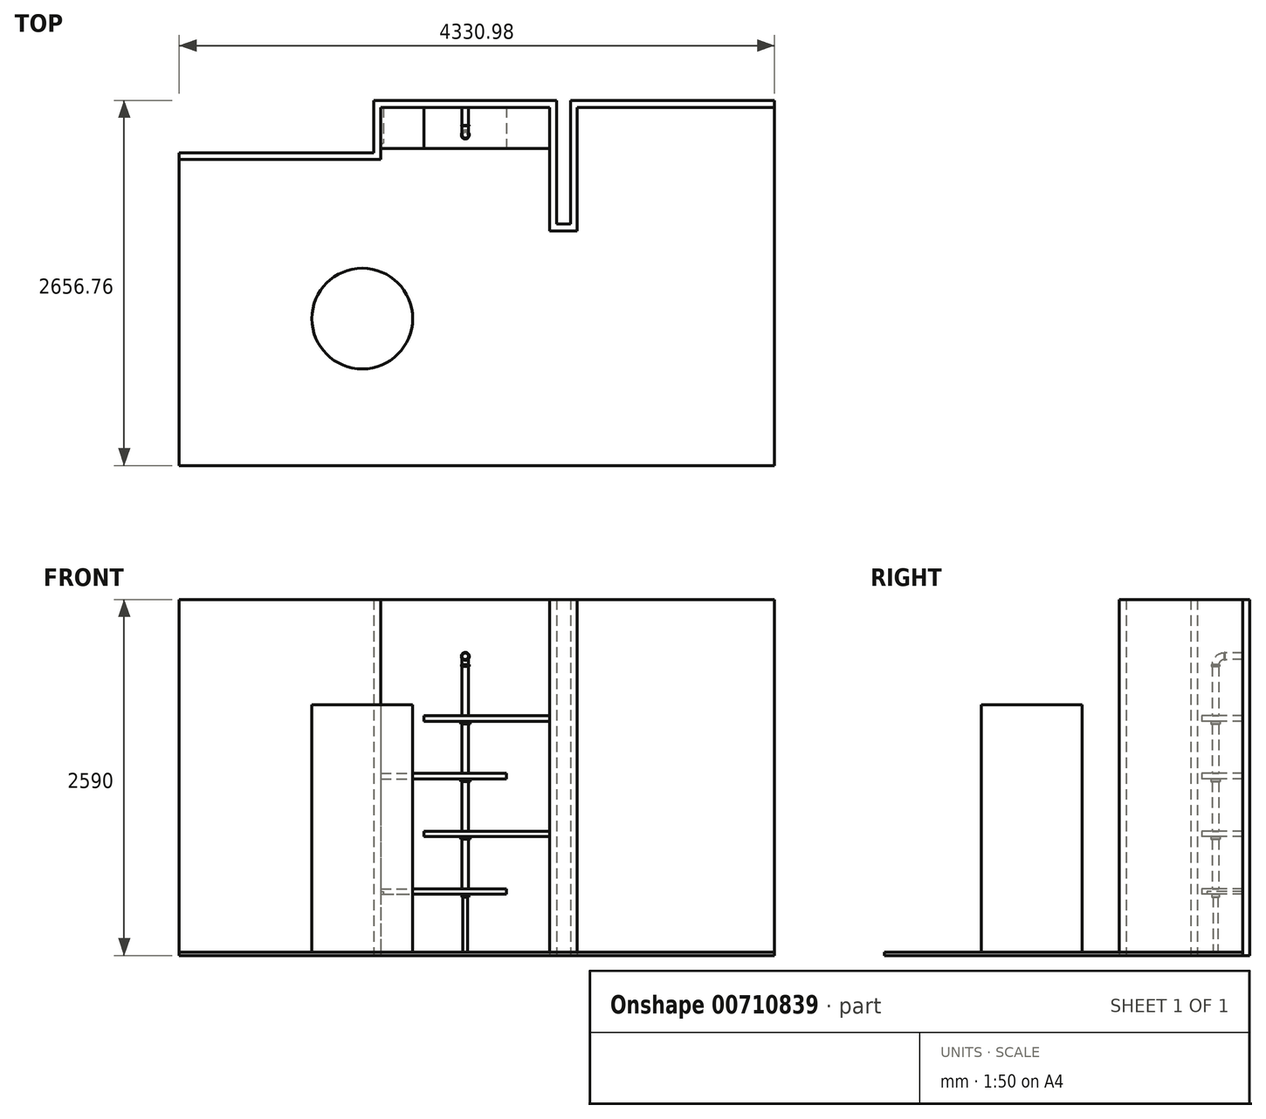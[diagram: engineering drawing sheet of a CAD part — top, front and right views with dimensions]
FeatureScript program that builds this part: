
annotation { "Feature Type Name" : "Feature", "Feature Type Description" : "" }
export const myFeature = defineFeature(function(context is Context, id is Id, definition is map)
    precondition{}
    {
        {
            var Q0;
            Q0=qCreatedBy(makeId("Top.planeOp"),FACE);
            var sketch = newSketch(context, id + "F0", { "sketchPlane" : qUnion([Q0])});
            skLineSegment(sketch, "E0", {"start": v(-2171.4, 181.95) * mm, "end": v(-705.2, 181.95) * mm});
            skLineSegment(sketch, "E1", {"start": v(-705.2, 181.95) * mm, "end": v(-705.2, 561.95) * mm});
            skLineSegment(sketch, "E2", {"start": v(-705.2, 561.95) * mm, "end": v(524.8, 561.95) * mm});
            skLineSegment(sketch, "E3", {"start": v(524.8, 561.95) * mm, "end": v(524.8, -338.05) * mm});
            skLineSegment(sketch, "E4", {"start": v(524.8, -338.05) * mm, "end": v(724.8, -338.05) * mm});
            skLineSegment(sketch, "E5", {"start": v(724.8, -338.05) * mm, "end": v(724.8, 561.95) * mm});
            skLineSegment(sketch, "E6", {"start": v(724.8, 561.95) * mm, "end": v(2159.6, 561.95) * mm});
            skLineSegment(sketch, "E7", {"start": v(2159.6, 561.95) * mm, "end": v(2159.6, -2044.81) * mm});
            skLineSegment(sketch, "E8", {"start": v(2159.6, -2044.81) * mm, "end": v(-2171.4, -2044.81) * mm});
            skLineSegment(sketch, "E9", {"start": v(-2171.4, -2044.81) * mm, "end": v(-2171.4, 181.95) * mm});
            skSolve(sketch);
        }
        {
            var Q0;
            Q0=makeQuery(id+"F0.imprint","IMPRINT",FACE,{"disambiguationData":[TD([[makeQuery(id+"F0.imprint","IMPRINT",EDGE,{"derivedFrom":sQuery(id+"F0.wireOp",EDGE,"E0")}),-1.0]])]});
            extrude(context, id + "F1", {"entities" : qUnion([Q0]), "depth" : 25 * mm, "offsetDistance" : 25 * mm});
        }
        {
            var Q0;
            Q0=makeQuery(id+"F1.opExtrude","CAP_FACE",FACE,{"disambiguationData":[OSD([sQuery(id+"F0.wireOp",EDGE,"E0"),sQuery(id+"F0.wireOp",EDGE,"E1"),sQuery(id+"F0.wireOp",EDGE,"E2"),sQuery(id+"F0.wireOp",EDGE,"E3"),sQuery(id+"F0.wireOp",EDGE,"E4"),sQuery(id+"F0.wireOp",EDGE,"E5"),sQuery(id+"F0.wireOp",EDGE,"E6"),sQuery(id+"F0.wireOp",EDGE,"E7"),sQuery(id+"F0.wireOp",EDGE,"E8"),sQuery(id+"F0.wireOp",EDGE,"E9")])],"isStart":true});
            var sketch = newSketch(context, id + "F2", { "sketchPlane" : qUnion([Q0])});
            skLineSegment(sketch, "E10", {"start": v(-2171.4, -181.95) * mm, "end": v(-705.2, -181.95) * mm});
            skLineSegment(sketch, "E11", {"start": v(-705.2, -181.95) * mm, "end": v(-705.2, -561.95) * mm});
            skLineSegment(sketch, "E12", {"start": v(-705.2, -561.95) * mm, "end": v(524.8, -561.95) * mm});
            skLineSegment(sketch, "E13", {"start": v(524.8, -561.95) * mm, "end": v(524.8, 338.05) * mm});
            skLineSegment(sketch, "E14", {"start": v(524.8, 338.05) * mm, "end": v(724.8, 338.05) * mm});
            skLineSegment(sketch, "E15", {"start": v(724.8, 338.05) * mm, "end": v(724.8, -561.95) * mm});
            skLineSegment(sketch, "E16", {"start": v(724.8, -561.95) * mm, "end": v(2159.6, -561.95) * mm});
            skLineSegment(sketch, "E17", {"start": v(2159.6, -561.95) * mm, "end": v(2159.6, -611.95) * mm});
            skLineSegment(sketch, "E18", {"start": v(2159.6, -611.95) * mm, "end": v(674.8, -611.95) * mm});
            skLineSegment(sketch, "E19", {"start": v(674.8, -611.95) * mm, "end": v(674.8, 288.05) * mm});
            skLineSegment(sketch, "E20", {"start": v(674.8, 288.05) * mm, "end": v(574.8, 288.05) * mm});
            skLineSegment(sketch, "E21", {"start": v(574.8, 288.05) * mm, "end": v(574.8, -611.95) * mm});
            skLineSegment(sketch, "E22", {"start": v(574.8, -611.95) * mm, "end": v(-755.2, -611.95) * mm});
            skLineSegment(sketch, "E23", {"start": v(-755.2, -611.95) * mm, "end": v(-755.2, -231.95) * mm});
            skLineSegment(sketch, "E24", {"start": v(-755.2, -231.95) * mm, "end": v(-2171.4, -231.95) * mm});
            skLineSegment(sketch, "E25", {"start": v(-2171.4, -231.95) * mm, "end": v(-2171.4, -181.95) * mm});
            skSolve(sketch);
        }
        {
            var Q0;
            Q0=makeQuery(id+"F2.imprint","IMPRINT",FACE,{"disambiguationData":[TD([[makeQuery(id+"F2.imprint","IMPRINT",EDGE,{"derivedFrom":sQuery(id+"F2.wireOp",EDGE,"E10")}),-1.0]])]});
            extrude(context, id + "F3", {"entities" : qUnion([Q0]), "oppositeDirection" : true, "depth" : 2590 * mm, "offsetDistance" : 25 * mm});
        }
        {
            var Q0;
            Q0=makeQuery(id+"F1.opExtrude","CAP_FACE",FACE,{"disambiguationData":[OSD([sQuery(id+"F0.wireOp",EDGE,"E0"),sQuery(id+"F0.wireOp",EDGE,"E1"),sQuery(id+"F0.wireOp",EDGE,"E2"),sQuery(id+"F0.wireOp",EDGE,"E3"),sQuery(id+"F0.wireOp",EDGE,"E4"),sQuery(id+"F0.wireOp",EDGE,"E5"),sQuery(id+"F0.wireOp",EDGE,"E6"),sQuery(id+"F0.wireOp",EDGE,"E7"),sQuery(id+"F0.wireOp",EDGE,"E8"),sQuery(id+"F0.wireOp",EDGE,"E9")])],"isStart":false});
            var sketch = newSketch(context, id + "F4", { "sketchPlane" : qUnion([Q0])});
            skLineSegment(sketch, "E26.bottom", {"start": v(-705.2, 561.95) * mm, "end": v(349.8, 561.95) * mm});
            skLineSegment(sketch, "E26.top", {"start": v(-705.2, 215.3) * mm, "end": v(349.8, 215.3) * mm});
            skLineSegment(sketch, "E26.left", {"start": v(-705.2, 561.95) * mm, "end": v(-705.2, 215.3) * mm});
            skLineSegment(sketch, "E26.right", {"start": v(349.8, 561.95) * mm, "end": v(349.8, 215.3) * mm});
            skCircle(sketch, "E27", {"center": v(-90.2, 361.95) * mm, "radius": 27 * mm});
            skPoint(sketch, "E27.centerSnap0", {"position": v(-90.2, 561.95) * mm});
            skSolve(sketch);
        }
        {
            var Q0;
            {var subQ3=sQuery(id+"F4.wireOp",EDGE,"E26.top");Q0=makeQuery(id+"F4.imprint","IMPRINT",FACE,{"disambiguationData":[TD([[makeQuery(id+"F4.imprint","IMPRINT",EDGE,{"derivedFrom":subQ3}),-1.0]])]});}
            cPlane(context, id + "F5", {"entities" : qUnion([Q0]), "cplaneType" : CPlaneType.OFFSET, "offset" : 420 * mm, "width" : 150 * mm, "height" : 150 * mm});
        }
        {
            var Q0;
            Q0=qCreatedBy(id+"F5.planeOp",FACE);
            cPlane(context, id + "F6", {"entities" : qUnion([Q0]), "cplaneType" : CPlaneType.OFFSET, "offset" : 420 * mm, "width" : 150 * mm, "height" : 150 * mm});
        }
        {
            var Q0;
            Q0=qCreatedBy(id+"F6.planeOp",FACE);
            cPlane(context, id + "F7", {"entities" : qUnion([Q0]), "cplaneType" : CPlaneType.OFFSET, "offset" : 420 * mm, "width" : 150 * mm, "height" : 150 * mm});
        }
        {
            var Q0;
            Q0=qCreatedBy(id+"F7.planeOp",FACE);
            cPlane(context, id + "F8", {"entities" : qUnion([Q0]), "cplaneType" : CPlaneType.OFFSET, "offset" : 420 * mm, "width" : 150 * mm, "height" : 150 * mm});
        }
        {
            var Q0;
            Q0=qCreatedBy(id+"F5.planeOp",FACE);
            var sketch = newSketch(context, id + "F9", { "sketchPlane" : qUnion([Q0])});
            skLineSegment(sketch, "E28.bottom", {"start": v(-705.2, 561.95) * mm, "end": v(209.8, 561.95) * mm});
            skLineSegment(sketch, "E28.top", {"start": v(-705.2, 261.95) * mm, "end": v(209.8, 261.95) * mm});
            skLineSegment(sketch, "E28.left", {"start": v(-705.2, 561.95) * mm, "end": v(-705.2, 261.95) * mm});
            skLineSegment(sketch, "E28.right", {"start": v(209.8, 561.95) * mm, "end": v(209.8, 261.95) * mm});
            skSolve(sketch);
        }
        {
            var Q0;
            Q0 = qSketchRegion(id + "F9", true);
            extrude(context, id + "F10", {"entities" : qUnion([Q0]), "depth" : 40 * mm, "offsetDistance" : 25 * mm});
        }
        {
            var Q0;
            Q0=qCreatedBy(id+"F6.planeOp",FACE);
            var sketch = newSketch(context, id + "F11", { "sketchPlane" : qUnion([Q0])});
            skLineSegment(sketch, "E29.bottom", {"start": v(524.8, 561.95) * mm, "end": v(-390.2, 561.95) * mm});
            skLineSegment(sketch, "E29.top", {"start": v(524.8, 261.95) * mm, "end": v(-390.2, 261.95) * mm});
            skLineSegment(sketch, "E29.left", {"start": v(524.8, 561.95) * mm, "end": v(524.8, 261.95) * mm});
            skLineSegment(sketch, "E29.right", {"start": v(-390.2, 561.95) * mm, "end": v(-390.2, 261.95) * mm});
            skSolve(sketch);
        }
        {
            var Q0;
            Q0 = qSketchRegion(id + "F11", true);
            extrude(context, id + "F12", {"entities" : qUnion([Q0]), "depth" : 40 * mm, "offsetDistance" : 25 * mm});
        }
        {
            var Q0;
            Q0=qCreatedBy(id+"F7.planeOp",FACE);
            var sketch = newSketch(context, id + "F13", { "sketchPlane" : qUnion([Q0])});
            skLineSegment(sketch, "E30.bottom", {"start": v(-705.2, 561.95) * mm, "end": v(209.8, 561.95) * mm});
            skLineSegment(sketch, "E30.top", {"start": v(-705.2, 261.95) * mm, "end": v(209.8, 261.95) * mm});
            skLineSegment(sketch, "E30.left", {"start": v(-705.2, 561.95) * mm, "end": v(-705.2, 261.95) * mm});
            skLineSegment(sketch, "E30.right", {"start": v(209.8, 561.95) * mm, "end": v(209.8, 261.95) * mm});
            skSolve(sketch);
        }
        {
            var Q0;
            Q0 = qSketchRegion(id + "F13", true);
            extrude(context, id + "F14", {"entities" : qUnion([Q0]), "depth" : 40 * mm, "offsetDistance" : 25 * mm});
        }
        {
            var Q0;
            Q0=qCreatedBy(id+"F8.planeOp",FACE);
            var sketch = newSketch(context, id + "F15", { "sketchPlane" : qUnion([Q0])});
            skLineSegment(sketch, "E31.bottom", {"start": v(524.8, 561.95) * mm, "end": v(-390.2, 561.95) * mm});
            skLineSegment(sketch, "E31.top", {"start": v(524.8, 261.95) * mm, "end": v(-390.2, 261.95) * mm});
            skLineSegment(sketch, "E31.left", {"start": v(524.8, 561.95) * mm, "end": v(524.8, 261.95) * mm});
            skLineSegment(sketch, "E31.right", {"start": v(-390.2, 561.95) * mm, "end": v(-390.2, 261.95) * mm});
            skSolve(sketch);
        }
        {
            var Q0;
            Q0 = qSketchRegion(id + "F15", true);
            extrude(context, id + "F16", {"entities" : qUnion([Q0]), "depth" : 40 * mm, "offsetDistance" : 25 * mm});
        }
        {
            var Q0;
            {var subQ3=sQuery(id+"F4.wireOp",EDGE,"E26.top");Q0=makeQuery(id+"F4.imprint","IMPRINT",FACE,{"disambiguationData":[TD([[makeQuery(id+"F4.imprint","IMPRINT",EDGE,{"derivedFrom":subQ3}),-1.0]])]});}
            var sketch = newSketch(context, id + "F17", { "sketchPlane" : qUnion([Q0])});
            skCircle(sketch, "E32", {"center": v(-90.2, 361.95) * mm, "radius": 18.15 * mm});
            skSolve(sketch);
        }
        {
            var Q0;
            Q0 = qSketchRegion(id + "F17", true);
            extrude(context, id + "F18", {"entities" : qUnion([Q0]), "depth" : 400 * mm, "offsetDistance" : 25 * mm});
        }
        {
            var Q0;
            Q0=makeQuery(id+"F16.opExtrude","CAP_FACE",FACE,{"disambiguationData":[OSD([sQuery(id+"F15.wireOp",EDGE,"E31.bottom"),sQuery(id+"F15.wireOp",EDGE,"E31.top"),sQuery(id+"F15.wireOp",EDGE,"E31.left"),sQuery(id+"F15.wireOp",EDGE,"E31.right")])],"isStart":false});
            var sketch = newSketch(context, id + "F19", { "sketchPlane" : qUnion([Q0])});
            skCircle(sketch, "E33", {"center": v(-90.2, 361.95) * mm, "radius": 24.15 * mm});
            skSolve(sketch);
        }
        {
            var Q0;
            Q0 = qSketchRegion(id + "F19", true);
            extrude(context, id + "F20", {"entities" : qUnion([Q0]), "operationType" : NewBodyOperationType.REMOVE, "oppositeDirection" : true, "depth" : 1320 * mm, "offsetDistance" : 25 * mm});
        }
        {
            var Q0;
            Q0=makeQuery(id+"F18.opExtrude","CAP_FACE",FACE,{"disambiguationData":[OSD([sQuery(id+"F17.wireOp",EDGE,"E32")])],"isStart":false});
            var sketch = newSketch(context, id + "F21", { "sketchPlane" : qUnion([Q0])});
            skCircle(sketch, "E34", {"center": v(-90.2, 361.95) * mm, "radius": 26 * mm});
            skSolve(sketch);
        }
        {
            var Q0;
            Q0 = qSketchRegion(id + "F21", true);
            extrude(context, id + "F22", {"entities" : qUnion([Q0]), "operationType" : NewBodyOperationType.ADD, "depth" : 20 * mm, "offsetDistance" : 25 * mm});
        }
        {
            var Q0;
            Q0=makeQuery(id+"F22.opExtrude","CAP_FACE",FACE,{"disambiguationData":[OSD([sQuery(id+"F21.wireOp",EDGE,"E34")])],"isStart":false});
            var sketch = newSketch(context, id + "F23", { "sketchPlane" : qUnion([Q0])});
            skCircle(sketch, "E35", {"center": v(-90.2, 361.95) * mm, "radius": 24.15 * mm});
            skSolve(sketch);
        }
        {
            var Q0;
            Q0 = qSketchRegion(id + "F23", true);
            extrude(context, id + "F24", {"entities" : qUnion([Q0]), "operationType" : NewBodyOperationType.ADD, "depth" : 400 * mm, "offsetDistance" : 25 * mm});
        }
        {
            var Q0;
            Q0=makeQuery(id+"F24.opExtrude","CAP_FACE",FACE,{"disambiguationData":[OSD([sQuery(id+"F23.wireOp",EDGE,"E35")])],"isStart":false});
            var sketch = newSketch(context, id + "F25", { "sketchPlane" : qUnion([Q0])});
            skCircle(sketch, "E36", {"center": v(-90.2, 361.95) * mm, "radius": 34.15 * mm});
            skSolve(sketch);
        }
        {
            var Q0;
            Q0 = qSketchRegion(id + "F25", true);
            extrude(context, id + "F26", {"entities" : qUnion([Q0]), "operationType" : NewBodyOperationType.ADD, "depth" : 20 * mm, "offsetDistance" : 25 * mm});
        }
        {
            var Q0;
            Q0=makeQuery(id+"F26.opExtrude","CAP_FACE",FACE,{"disambiguationData":[OSD([sQuery(id+"F25.wireOp",EDGE,"E36")])],"isStart":false});
            var sketch = newSketch(context, id + "F27", { "sketchPlane" : qUnion([Q0])});
            skCircle(sketch, "E37", {"center": v(-90.2, 361.95) * mm, "radius": 24.15 * mm});
            skSolve(sketch);
        }
        {
            var Q0;
            Q0 = qSketchRegion(id + "F27", true);
            extrude(context, id + "F28", {"entities" : qUnion([Q0]), "operationType" : NewBodyOperationType.ADD, "depth" : 400 * mm, "offsetDistance" : 25 * mm});
        }
        {
            var Q0;
            Q0=makeQuery(id+"F28.opExtrude","CAP_FACE",FACE,{"disambiguationData":[OSD([sQuery(id+"F27.wireOp",EDGE,"E37")])],"isStart":false});
            var sketch = newSketch(context, id + "F29", { "sketchPlane" : qUnion([Q0])});
            skCircle(sketch, "E38", {"center": v(-90.2, 361.95) * mm, "radius": 34.15 * mm});
            skSolve(sketch);
        }
        {
            var Q0;
            Q0 = qSketchRegion(id + "F29", true);
            extrude(context, id + "F30", {"entities" : qUnion([Q0]), "operationType" : NewBodyOperationType.ADD, "depth" : 20 * mm, "offsetDistance" : 25 * mm});
        }
        {
            var Q0;
            Q0=makeQuery(id+"F30.opExtrude","CAP_FACE",FACE,{"disambiguationData":[OSD([sQuery(id+"F29.wireOp",EDGE,"E38")])],"isStart":false});
            var sketch = newSketch(context, id + "F31", { "sketchPlane" : qUnion([Q0])});
            skCircle(sketch, "E39", {"center": v(-90.2, 361.95) * mm, "radius": 24.15 * mm});
            skSolve(sketch);
        }
        {
            var Q0;
            Q0 = qSketchRegion(id + "F31", true);
            extrude(context, id + "F32", {"entities" : qUnion([Q0]), "operationType" : NewBodyOperationType.ADD, "depth" : 400 * mm, "offsetDistance" : 25 * mm});
        }
        {
            var Q0;
            Q0=makeQuery(id+"F32.opExtrude","CAP_FACE",FACE,{"disambiguationData":[OSD([sQuery(id+"F31.wireOp",EDGE,"E39")])],"isStart":false});
            var sketch = newSketch(context, id + "F33", { "sketchPlane" : qUnion([Q0])});
            skCircle(sketch, "E40", {"center": v(-90.2, 361.95) * mm, "radius": 34.15 * mm});
            skSolve(sketch);
        }
        {
            var Q0;
            Q0 = qSketchRegion(id + "F33", true);
            extrude(context, id + "F34", {"entities" : qUnion([Q0]), "operationType" : NewBodyOperationType.ADD, "depth" : 20 * mm, "offsetDistance" : 25 * mm});
        }
        {
            var Q0;
            Q0=makeQuery(id+"F34.opExtrude","CAP_FACE",FACE,{"disambiguationData":[OSD([sQuery(id+"F33.wireOp",EDGE,"E40")])],"isStart":false});
            var sketch = newSketch(context, id + "F35", { "sketchPlane" : qUnion([Q0])});
            skCircle(sketch, "E41", {"center": v(-90.2, 361.95) * mm, "radius": 24.15 * mm});
            skSolve(sketch);
        }
        {
            var Q0;
            Q0 = qSketchRegion(id + "F35", true);
            extrude(context, id + "F36", {"entities" : qUnion([Q0]), "operationType" : NewBodyOperationType.ADD, "depth" : 400 * mm, "offsetDistance" : 25 * mm});
        }
        {
            var Q0;
            Q0=makeQuery(id+"F36.opExtrude","CAP_FACE",FACE,{"disambiguationData":[OSD([sQuery(id+"F35.wireOp",EDGE,"E41")])],"isStart":false});
            var sketch = newSketch(context, id + "F37", { "sketchPlane" : qUnion([Q0])});
            skCircle(sketch, "E42", {"center": v(-90.2, 361.95) * mm, "radius": 29.15 * mm});
            skSolve(sketch);
        }
        {
            var Q0;
            Q0 = qSketchRegion(id + "F37", true);
            extrude(context, id + "F38", {"entities" : qUnion([Q0]), "operationType" : NewBodyOperationType.ADD, "depth" : 10 * mm, "offsetDistance" : 25 * mm});
        }
        {
            var Q0;
            Q0=makeQuery(id+"F38.opExtrude","CAP_FACE",FACE,{"disambiguationData":[OSD([sQuery(id+"F37.wireOp",EDGE,"E42")])],"isStart":false});
            cPlane(context, id + "F39", {"entities" : qUnion([Q0]), "cplaneType" : CPlaneType.OFFSET, "offset" : 25 * mm, "width" : 150 * mm, "height" : 150 * mm});
        }
        {
            var Q0;
            Q0=qCreatedBy(id+"F39.planeOp",FACE);
            var sketch = newSketch(context, id + "F40", { "sketchPlane" : qUnion([Q0])});
            skLineSegment(sketch, "E43", {"start": v(-110.65, 396.1) * mm, "end": v(-103.04, 396.1) * mm});
            skSolve(sketch);
        }
        {
            var Q0;
            Q0=qCreatedBy(id+"F39.planeOp",FACE);
            var Q1;
            Q1=sQuery(id+"F40.wireOp",EDGE,"E43");
            cPlane(context, id + "F41", {"entities" : qUnion([Q0, Q1]), "cplaneType" : CPlaneType.LINE_ANGLE, "offset" : 25 * mm, "angle" : 90 * degree, "width" : 150 * mm, "height" : 150 * mm});
        }
        {
            var Q0;
            Q0=makeQuery(id+"F38.opExtrude","CAP_FACE",FACE,{"disambiguationData":[OSD([sQuery(id+"F37.wireOp",EDGE,"E42")])],"isStart":false});
            var sketch = newSketch(context, id + "F42", { "sketchPlane" : qUnion([Q0])});
            skCircle(sketch, "E44", {"center": v(-90.2, 361.95) * mm, "radius": 24.15 * mm});
            skSolve(sketch);
        }
        {
            var Q0;
            Q0=qCreatedBy(id+"F39.planeOp",FACE);
            var sketch = newSketch(context, id + "F43", { "sketchPlane" : qUnion([Q0])});
            skLineSegment(sketch, "E45", {"start": v(-90.2, 347.92) * mm, "end": v(-90.2, 375.23) * mm});
            skSolve(sketch);
        }
        {
            var Q0;
            Q0=qCreatedBy(id+"F39.planeOp",FACE);
            var Q1;
            Q1=sQuery(id+"F43.wireOp",EDGE,"E45");
            cPlane(context, id + "F44", {"entities" : qUnion([Q0, Q1]), "cplaneType" : CPlaneType.LINE_ANGLE, "offset" : 25 * mm, "angle" : 90 * degree, "width" : 150 * mm, "height" : 150 * mm});
        }
        {
            var Q0;
            Q0=qCreatedBy(id+"F44.planeOp",FACE);
            var sketch = newSketch(context, id + "F45", { "sketchPlane" : qUnion([Q0])});
            skArc(sketch, "E46", {"start": v(-361.95, 2115) * mm, "mid": v(-381.8, 2159.12) * mm, "end": v(-426.95, 2176.53) * mm});
            skSolve(sketch);
        }
        {
            var Q0;
            Q0=makeQuery(id+"F42.imprint","IMPRINT",FACE,{"disambiguationData":[TD([[makeQuery(id+"F42.imprint","IMPRINT",EDGE,{"derivedFrom":sQuery(id+"F42.wireOp",EDGE,"E44")}),1.0]])]});
            var Q1;
            Q1=sQuery(id+"F45.wireOp",EDGE,"E46");
            sweep(context, id + "F46", {"operationType" : NewBodyOperationType.ADD, "profiles" : qUnion([Q0]), "path" : qUnion([Q1])});
        }
        {
            var Q0;
            Q0=makeQuery(id+"F46.opSweep","CAP_FACE",FACE,{"disambiguationData":[OSD([sQuery(id+"F42.wireOp",EDGE,"E44"),sQuery(id+"F45.wireOp",VERTEX,"E46.end")])],"isStart":false});
            var sketch = newSketch(context, id + "F47", { "sketchPlane" : qUnion([Q0])});
            skCircle(sketch, "E47", {"center": v(90.2, 2171.73) * mm, "radius": 29.15 * mm});
            skSolve(sketch);
        }
        {
            var Q0;
            Q0 = qSketchRegion(id + "F47", true);
            extrude(context, id + "F48", {"entities" : qUnion([Q0]), "operationType" : NewBodyOperationType.ADD, "depth" : 5 * mm, "offsetDistance" : 25 * mm});
        }
        {
            var Q0;
            Q0=makeQuery(id+"F48.opExtrude","CAP_FACE",FACE,{"disambiguationData":[OSD([sQuery(id+"F47.wireOp",EDGE,"E47")])],"isStart":false});
            var sketch = newSketch(context, id + "F49", { "sketchPlane" : qUnion([Q0])});
            skCircle(sketch, "E48", {"center": v(90.2, 2171.73) * mm, "radius": 24.15 * mm});
            skSolve(sketch);
        }
        {
            var Q0;
            Q0 = qSketchRegion(id + "F49", true);
            var Q1;
            Q1=makeQuery(id+"F3.opExtrude","SWEPT_FACE",FACE,{"disambiguationData":[OSD([sQuery(id+"F2.wireOp",EDGE,"E12")])]});
            extrude(context, id + "F50", {"entities" : qUnion([Q0]), "operationType" : NewBodyOperationType.ADD, "endBound" : BoundingType.UP_TO_SURFACE, "depth" : 25 * mm, "endBoundEntityFace" : qUnion([Q1]), "offsetDistance" : 25 * mm});
        }
        {
            var Q0;
            Q0=makeQuery(id+"F1.opExtrude","CAP_FACE",FACE,{"disambiguationData":[OSD([sQuery(id+"F0.wireOp",EDGE,"E0"),sQuery(id+"F0.wireOp",EDGE,"E1"),sQuery(id+"F0.wireOp",EDGE,"E2"),sQuery(id+"F0.wireOp",EDGE,"E3"),sQuery(id+"F0.wireOp",EDGE,"E4"),sQuery(id+"F0.wireOp",EDGE,"E5"),sQuery(id+"F0.wireOp",EDGE,"E6"),sQuery(id+"F0.wireOp",EDGE,"E7"),sQuery(id+"F0.wireOp",EDGE,"E8"),sQuery(id+"F0.wireOp",EDGE,"E9")])],"isStart":false});
            var sketch = newSketch(context, id + "F51", { "sketchPlane" : qUnion([Q0])});
            skCircle(sketch, "E49", {"center": v(-839.62, -975.1) * mm, "radius": 366.44 * mm});
            skSolve(sketch);
        }
        {
            var Q0;
            Q0=makeQuery(id+"F51.imprint","IMPRINT",FACE,{"disambiguationData":[TD([[makeQuery(id+"F51.imprint","IMPRINT",EDGE,{"derivedFrom":sQuery(id+"F51.wireOp",EDGE,"E49")}),1.0]])]});
            extrude(context, id + "F52", {"entities" : qUnion([Q0]), "depth" : 1800 * mm, "offsetDistance" : 25 * mm});
        }
        {
            var Q0;
            Q0=makeQuery(id+"F10.opExtrude","CAP_FACE",FACE,{"disambiguationData":[OSD([sQuery(id+"F9.wireOp",EDGE,"E28.bottom"),sQuery(id+"F9.wireOp",EDGE,"E28.top"),sQuery(id+"F9.wireOp",EDGE,"E28.left"),sQuery(id+"F9.wireOp",EDGE,"E28.right")])],"isStart":true});
            var sketch = newSketch(context, id + "F53", { "sketchPlane" : qUnion([Q0])});
            skLineSegment(sketch, "E50.bottom", {"start": v(-705.2, -561.95) * mm, "end": v(-685.2, -561.95) * mm});
            skLineSegment(sketch, "E50.top", {"start": v(-705.2, -301.95) * mm, "end": v(-685.2, -301.95) * mm});
            skLineSegment(sketch, "E50.left", {"start": v(-705.2, -561.95) * mm, "end": v(-705.2, -301.95) * mm});
            skLineSegment(sketch, "E50.right", {"start": v(-685.2, -561.95) * mm, "end": v(-685.2, -301.95) * mm});
            skSolve(sketch);
        }
        {
            var Q0;
            Q0=makeQuery(id+"F53.imprint","IMPRINT",FACE,{"disambiguationData":[TD([[makeQuery(id+"F53.imprint","IMPRINT",EDGE,{"derivedFrom":sQuery(id+"F53.wireOp",EDGE,"E50.bottom")}),1.0]])]});
            extrude(context, id + "F54", {"entities" : qUnion([Q0]), "operationType" : NewBodyOperationType.REMOVE, "oppositeDirection" : true, "depth" : 20 * mm, "offsetDistance" : 25 * mm});
        }
    });
